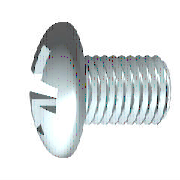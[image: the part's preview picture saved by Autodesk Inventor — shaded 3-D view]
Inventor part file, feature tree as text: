
AUTODESK INVENTOR PART (.ipt)
format: ipt  version: 2024 (Build 280153000, 153)  size: 261,120 bytes
history: native  units: mm (DEFAULTED — no unit token found)
features: extrude x1, other x1, plane x1
ambient origin geometry x7: Origin, YZ Plane, XZ Plane, X Axis, Y Axis, Z Axis, Center Point
bodies: Solid1 (feature_tree), Body (feature_tree)
feature tree (3):
  extrude  "Slot"  Depth=3.0mm
  other  "Cut"
  plane  "Work Plane3"
